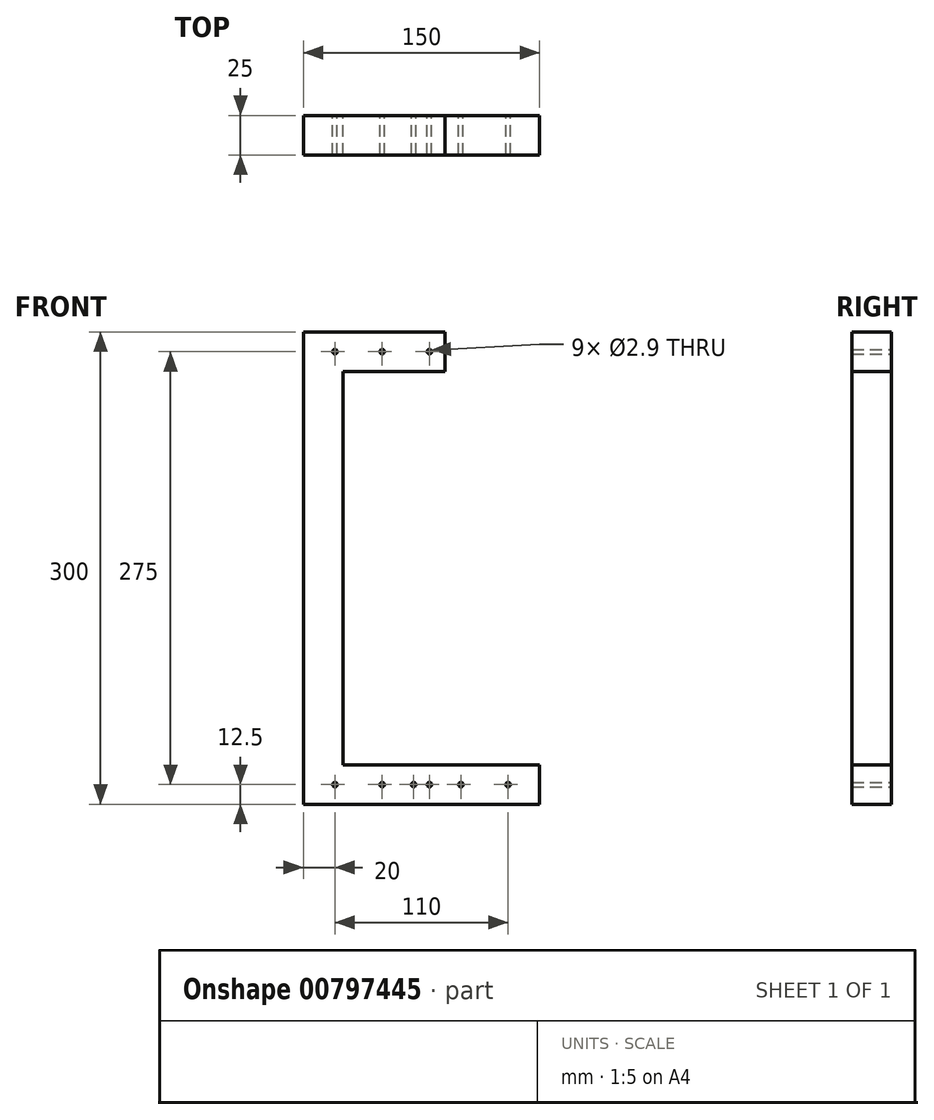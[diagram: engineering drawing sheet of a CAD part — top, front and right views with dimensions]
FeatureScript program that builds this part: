
annotation { "Feature Type Name" : "Feature", "Feature Type Description" : "" }
export const myFeature = defineFeature(function(context is Context, id is Id, definition is map)
    precondition{}
    {
        {
            var Q0;
            Q0=qCreatedBy(makeId("Front.planeOp"),FACE);
            var sketch = newSketch(context, id + "F0", { "sketchPlane" : qUnion([Q0])});
            skLineSegment(sketch, "E0.bottom", {"start": v(-120, 150) * mm, "end": v(-30, 150) * mm});
            skLineSegment(sketch, "E0.top", {"start": v(-120, -150) * mm, "end": v(30, -150) * mm});
            skLineSegment(sketch, "E0.left", {"start": v(-120, 150) * mm, "end": v(-120, -150) * mm});
            skPoint(sketch, "E0.middle", {"position": v(0, 0) * mm});
            skLineSegment(sketch, "E1.0", {"start": v(-95, 125) * mm, "end": v(-30, 125) * mm});
            skLineSegment(sketch, "E1.1", {"start": v(-95, 125) * mm, "end": v(-95, -125) * mm});
            skLineSegment(sketch, "E1.2", {"start": v(-95, -125) * mm, "end": v(30, -125) * mm});
            skLineSegment(sketch, "E2", {"start": v(-30, 125) * mm, "end": v(-30, 150) * mm});
            skLineSegment(sketch, "E3", {"start": v(30, -125) * mm, "end": v(30, -150) * mm});
            skLineSegment(sketch, "E4", {"start": v(-30, 137.5) * mm, "end": v(-132.37, 137.5) * mm, "construction": true});
            skLineSegment(sketch, "E5", {"start": v(30, -137.5) * mm, "end": v(138.86, -137.5) * mm, "construction": true});
            skCircle(sketch, "E6", {"center": v(-40, 137.5) * mm, "radius": 1.45 * mm});
            skCircle(sketch, "E7", {"center": v(-70, 137.5) * mm, "radius": 1.45 * mm});
            skCircle(sketch, "E8.1.0.0", {"center": v(-100, 137.5) * mm, "radius": 1.45 * mm});
            skLineSegment(sketch, "E8.direction1", {"start": v(-70, 137.5) * mm, "end": v(-100, 137.5) * mm, "construction": true});
            skLineSegment(sketch, "E9", {"start": v(0, 0) * mm, "end": v(148.9, 0) * mm, "construction": true});
            skLineSegment(sketch, "E10", {"start": v(0, 0) * mm, "end": v(0, 94.45) * mm, "construction": true});
            skCircle(sketch, "E11.MirrorC", {"center": v(-100, -137.5) * mm, "radius": 1.45 * mm});
            skCircle(sketch, "E12.MirrorC", {"center": v(-70, -137.5) * mm, "radius": 1.45 * mm});
            skCircle(sketch, "E13.MirrorC", {"center": v(-40, -137.5) * mm, "radius": 1.45 * mm});
            skCircle(sketch, "E14", {"center": v(10, -137.5) * mm, "radius": 1.45 * mm});
            skCircle(sketch, "E15.1.0.0", {"center": v(-20, -137.5) * mm, "radius": 1.45 * mm});
            skCircle(sketch, "E15.2.0.0", {"center": v(-50, -137.5) * mm, "radius": 1.45 * mm});
            skLineSegment(sketch, "E15.direction1", {"start": v(10, -137.5) * mm, "end": v(-20, -137.5) * mm, "construction": true});
            skSolve(sketch);
        }
        {
            var Q0;
            Q0 = qSketchRegion(id + "F0", true);
            extrude(context, id + "F1", {"entities" : qUnion([Q0]), "depth" : 25 * mm, "offsetDistance" : 25 * mm});
        }
    });
